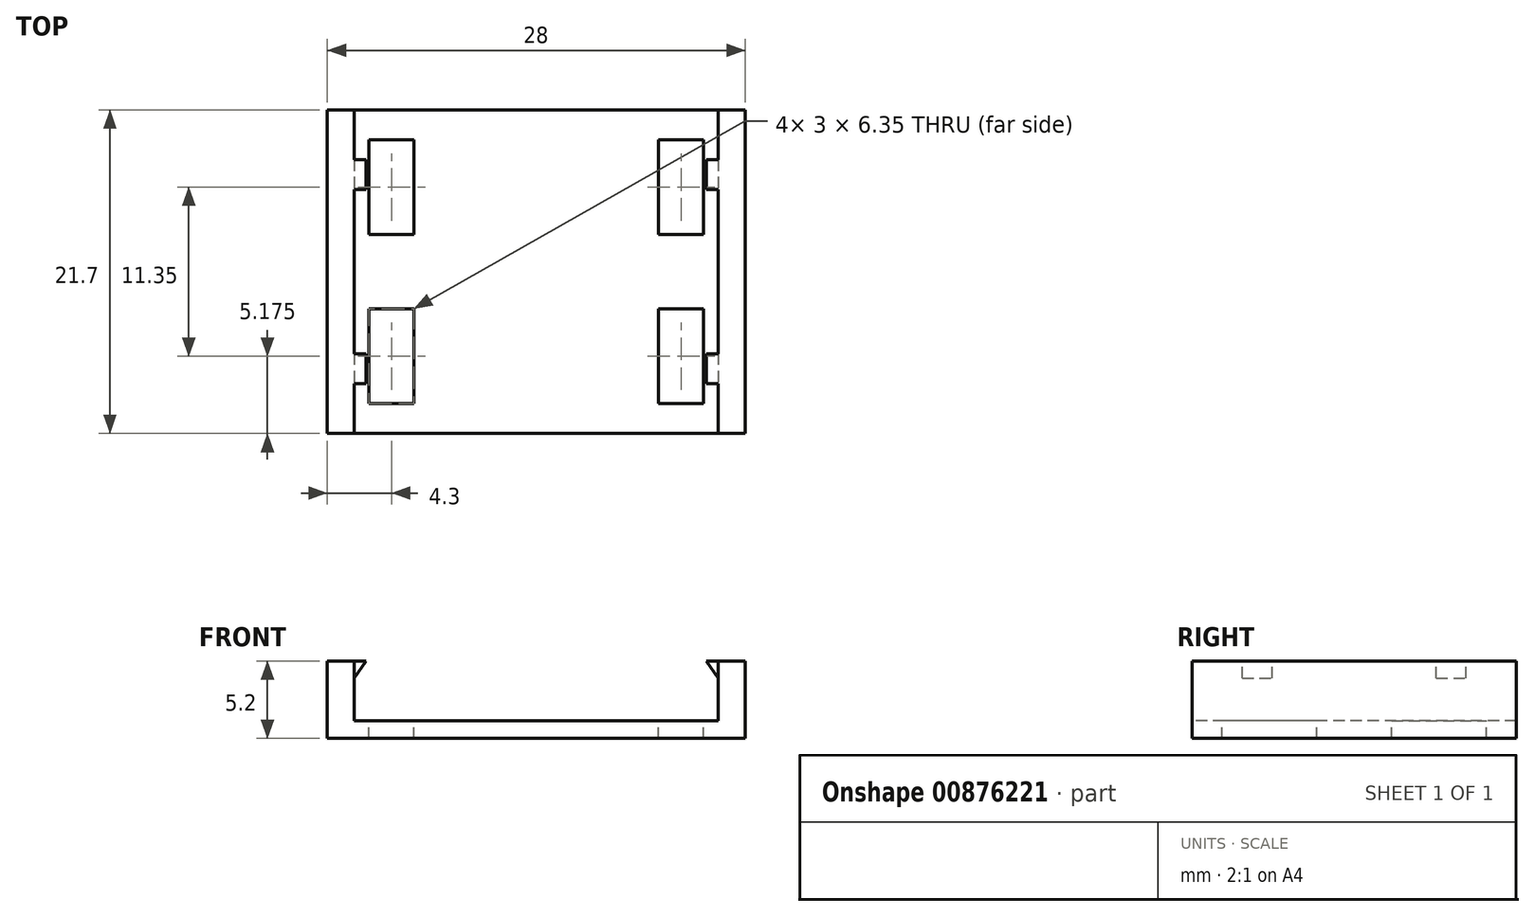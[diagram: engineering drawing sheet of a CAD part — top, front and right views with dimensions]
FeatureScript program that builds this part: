
annotation { "Feature Type Name" : "Feature", "Feature Type Description" : "" }
export const myFeature = defineFeature(function(context is Context, id is Id, definition is map)
    precondition{}
    {
        {
            var Q0;
            Q0=qCreatedBy(makeId("Top.planeOp"),FACE);
            var sketch = newSketch(context, id + "F0", { "sketchPlane" : qUnion([Q0])});
            skLineSegment(sketch, "E0.bottom", {"start": v(-14, 16.35) * mm, "end": v(14, 16.35) * mm});
            skLineSegment(sketch, "E0.top", {"start": v(-14, -16.35) * mm, "end": v(14, -16.35) * mm});
            skLineSegment(sketch, "E0.left", {"start": v(-14, 16.35) * mm, "end": v(-14, -16.35) * mm});
            skLineSegment(sketch, "E0.right", {"start": v(14, 16.35) * mm, "end": v(14, -16.35) * mm});
            skPoint(sketch, "E0.middle", {"position": v(0, 0) * mm});
            skSolve(sketch);
        }
        {
            var Q0;
            Q0=makeQuery(id+"F0.imprint","IMPRINT",FACE,{"disambiguationData":[TD([[makeQuery(id+"F0.imprint","IMPRINT",EDGE,{"derivedFrom":sQuery(id+"F0.wireOp",EDGE,"E0.bottom")}),-1.0]])]});
            extrude(context, id + "F1", {"entities" : qUnion([Q0]), "depth" : 1.2 * mm});
        }
        {
            var Q0;
            {var subQ5=sQuery(id+"F0.wireOp",EDGE,"E0.right");var subQ6=sQuery(id+"F0.wireOp",EDGE,"E0.left");var subQ7=sQuery(id+"F0.wireOp",EDGE,"E0.top");var subQ8=sQuery(id+"F0.wireOp",EDGE,"E0.bottom");var subQ9=makeQuery(id+"F1.opExtrude","CAP_FACE",FACE,{"disambiguationData":[OSD([subQ8,subQ7,subQ6,subQ5])],"isStart":false});var subQ12=subQ9;Q0=makeQuery(id+"FTskU3KK5imesQs_1.opFillet","MERGE",FACE,{"derivedFrom":[makeQuery(id+"FZi3CJKkktuihJ1_1.boolean.opBoolean","SPLIT",FACE,{"disambiguationData":[TD([makeQuery(id+"F1.opExtrude","SWEPT_FACE",FACE,{"disambiguationData":[OSD([subQ8])]})])],"derivedFrom":subQ12}),makeQuery(id+"FZ7EBSF1tdb4njM_1.boolean.opBoolean","MERGE",FACE,{"derivedFrom":[makeQuery(id+"FZi3CJKkktuihJ1_1.boolean.opBoolean","SPLIT",FACE,{"disambiguationData":[TD([makeQuery(id+"FlsG0jWeIkAughT_1.opExtrude","SWEPT_FACE",FACE,{"disambiguationData":[OSD([sQuery(id+"F5Wyuop6bpOGen8_1.wireOp",EDGE,"vaNtV44L-idVL-UOBQ-HHhe-vYpkaX2QMto8.bottom")])]})])],"derivedFrom":subQ12}),makeQuery(id+"FZ7EBSF1tdb4njM_1.opExtrude","CAP_FACE",FACE,{"disambiguationData":[OSD([sQuery(id+"FoSm93bD1NxVTFu_1.wireOp",EDGE,"97a7e462-43fe-4127-a601-1d90c2ab95a00.MirrorCS"),sQuery(id+"FoSm93bD1NxVTFu_1.wireOp",EDGE,"97a7e462-43fe-4127-a601-1d90c2ab95a01.MirrorCS"),sQuery(id+"FoSm93bD1NxVTFu_1.wireOp",EDGE,"97a7e462-43fe-4127-a601-1d90c2ab95a02.MirrorCS"),sQuery(id+"FoSm93bD1NxVTFu_1.wireOp",EDGE,"97a7e462-43fe-4127-a601-1d90c2ab95a03.MirrorCS")])],"isStart":false})]}),makeQuery(id+"FZ7EBSF1tdb4njM_1.boolean.opBoolean","MERGE",FACE,{"derivedFrom":[makeQuery(id+"FZi3CJKkktuihJ1_1.boolean.opBoolean","SPLIT",FACE,{"disambiguationData":[TD([makeQuery(id+"FlsG0jWeIkAughT_1.opExtrude","SWEPT_FACE",FACE,{"disambiguationData":[OSD([sQuery(id+"F5Wyuop6bpOGen8_1.wireOp",EDGE,"5b2c8ccd-c1e1-48dd-aecc-73c440124aab0.MirrorCS")])]})])],"derivedFrom":subQ12}),makeQuery(id+"FZ7EBSF1tdb4njM_1.opExtrude","CAP_FACE",FACE,{"disambiguationData":[OSD([sQuery(id+"FoSm93bD1NxVTFu_1.wireOp",EDGE,"85c03d27-702a-4580-8be8-e1d3315b53173.MirrorCS"),sQuery(id+"FoSm93bD1NxVTFu_1.wireOp",EDGE,"85c03d27-702a-4580-8be8-e1d3315b53174.MirrorCS"),sQuery(id+"FoSm93bD1NxVTFu_1.wireOp",EDGE,"85c03d27-702a-4580-8be8-e1d3315b53176.MirrorCS"),sQuery(id+"FoSm93bD1NxVTFu_1.wireOp",EDGE,"85c03d27-702a-4580-8be8-e1d3315b53177.MirrorCS")])],"isStart":false})]})]});}
            var sketch = newSketch(context, id + "F2", { "sketchPlane" : qUnion([Q0])});
            skLineSegment(sketch, "E1.bottom", {"start": v(-12.2, 15.35) * mm, "end": v(12.2, 15.35) * mm});
            skLineSegment(sketch, "E1.top", {"start": v(-12.2, -15.35) * mm, "end": v(12.2, -15.35) * mm});
            skLineSegment(sketch, "E1.left", {"start": v(-12.2, 15.35) * mm, "end": v(-12.2, -15.35) * mm});
            skLineSegment(sketch, "E1.right", {"start": v(12.2, 15.35) * mm, "end": v(12.2, -15.35) * mm});
            skPoint(sketch, "E1.middle", {"position": v(0, 0) * mm});
            skSolve(sketch);
        }
        {
            var Q0;
            Q0=makeQuery(id+"F2.imprint","IMPRINT",FACE,{"disambiguationData":[TD([[makeQuery(id+"F2.imprint","IMPRINT",EDGE,{"derivedFrom":sQuery(id+"F2.wireOp",EDGE,"E1.bottom")}),1.0]])]});
            extrude(context, id + "F3", {"entities" : qUnion([Q0]), "operationType" : NewBodyOperationType.ADD, "depth" : 4 * mm});
        }
        {
            var Q0;
            Q0=makeQuery(id+"F3.opExtrude","CAP_FACE",FACE,{"disambiguationData":[OSD([sQuery(id+"F0.wireOp",EDGE,"E0.bottom"),sQuery(id+"F0.wireOp",EDGE,"E0.top"),sQuery(id+"F0.wireOp",EDGE,"E0.left"),sQuery(id+"F0.wireOp",EDGE,"E0.right"),sQuery(id+"F2.wireOp",EDGE,"E1.bottom"),sQuery(id+"F2.wireOp",EDGE,"E1.top"),sQuery(id+"F2.wireOp",EDGE,"E1.left"),sQuery(id+"F2.wireOp",EDGE,"E1.right")])],"isStart":false});
            var sketch = newSketch(context, id + "F4", { "sketchPlane" : qUnion([Q0])});
            skLineSegment(sketch, "E2.bottom", {"start": v(-14, -16.35) * mm, "end": v(14, -16.35) * mm});
            skLineSegment(sketch, "E2.top", {"start": v(-14, -10.85) * mm, "end": v(14, -10.85) * mm});
            skLineSegment(sketch, "E2.left", {"start": v(-14, -16.35) * mm, "end": v(-14, -10.85) * mm});
            skLineSegment(sketch, "E2.right", {"start": v(14, -16.35) * mm, "end": v(14, -10.85) * mm});
            skLineSegment(sketch, "E3.MirrorCS", {"start": v(14, 16.35) * mm, "end": v(14, 10.85) * mm});
            skLineSegment(sketch, "E4.MirrorCS", {"start": v(-14, 16.35) * mm, "end": v(-14, 10.85) * mm});
            skLineSegment(sketch, "E5.MirrorCS", {"start": v(-14, 16.35) * mm, "end": v(14, 16.35) * mm});
            skLineSegment(sketch, "E6.MirrorCS", {"start": v(-14, 10.85) * mm, "end": v(14, 10.85) * mm});
            skSolve(sketch);
        }
        {
            var Q0;
            Q0=qSketchRegion(id+"F4",true);
            extrude(context, id + "F5", {"entities" : qUnion([Q0]), "operationType" : NewBodyOperationType.REMOVE, "endBound" : BoundingType.THROUGH_ALL, "oppositeDirection" : true, "depth" : 25 * mm});
        }
        {
            var Q0;
            {var subQ5=sQuery(id+"F0.wireOp",EDGE,"E0.right");var subQ6=sQuery(id+"F0.wireOp",EDGE,"E0.left");var subQ7=sQuery(id+"F0.wireOp",EDGE,"E0.top");var subQ8=sQuery(id+"F0.wireOp",EDGE,"E0.bottom");var subQ9=makeQuery(id+"F1.opExtrude","CAP_FACE",FACE,{"disambiguationData":[OSD([subQ8,subQ7,subQ6,subQ5])],"isStart":false});var subQ12=subQ9;Q0=makeQuery(id+"FTskU3KK5imesQs_1.opFillet","MERGE",FACE,{"derivedFrom":[makeQuery(id+"FZi3CJKkktuihJ1_1.boolean.opBoolean","SPLIT",FACE,{"disambiguationData":[TD([makeQuery(id+"F1.opExtrude","SWEPT_FACE",FACE,{"disambiguationData":[OSD([subQ8])]})])],"derivedFrom":subQ12}),makeQuery(id+"FZ7EBSF1tdb4njM_1.boolean.opBoolean","MERGE",FACE,{"derivedFrom":[makeQuery(id+"FZi3CJKkktuihJ1_1.boolean.opBoolean","SPLIT",FACE,{"disambiguationData":[TD([makeQuery(id+"FlsG0jWeIkAughT_1.opExtrude","SWEPT_FACE",FACE,{"disambiguationData":[OSD([sQuery(id+"F5Wyuop6bpOGen8_1.wireOp",EDGE,"vaNtV44L-idVL-UOBQ-HHhe-vYpkaX2QMto8.bottom")])]})])],"derivedFrom":subQ12}),makeQuery(id+"FZ7EBSF1tdb4njM_1.opExtrude","CAP_FACE",FACE,{"disambiguationData":[OSD([sQuery(id+"FoSm93bD1NxVTFu_1.wireOp",EDGE,"97a7e462-43fe-4127-a601-1d90c2ab95a00.MirrorCS"),sQuery(id+"FoSm93bD1NxVTFu_1.wireOp",EDGE,"97a7e462-43fe-4127-a601-1d90c2ab95a01.MirrorCS"),sQuery(id+"FoSm93bD1NxVTFu_1.wireOp",EDGE,"97a7e462-43fe-4127-a601-1d90c2ab95a02.MirrorCS"),sQuery(id+"FoSm93bD1NxVTFu_1.wireOp",EDGE,"97a7e462-43fe-4127-a601-1d90c2ab95a03.MirrorCS")])],"isStart":false})]}),makeQuery(id+"FZ7EBSF1tdb4njM_1.boolean.opBoolean","MERGE",FACE,{"derivedFrom":[makeQuery(id+"FZi3CJKkktuihJ1_1.boolean.opBoolean","SPLIT",FACE,{"disambiguationData":[TD([makeQuery(id+"FlsG0jWeIkAughT_1.opExtrude","SWEPT_FACE",FACE,{"disambiguationData":[OSD([sQuery(id+"F5Wyuop6bpOGen8_1.wireOp",EDGE,"5b2c8ccd-c1e1-48dd-aecc-73c440124aab0.MirrorCS")])]})])],"derivedFrom":subQ12}),makeQuery(id+"FZ7EBSF1tdb4njM_1.opExtrude","CAP_FACE",FACE,{"disambiguationData":[OSD([sQuery(id+"FoSm93bD1NxVTFu_1.wireOp",EDGE,"85c03d27-702a-4580-8be8-e1d3315b53173.MirrorCS"),sQuery(id+"FoSm93bD1NxVTFu_1.wireOp",EDGE,"85c03d27-702a-4580-8be8-e1d3315b53174.MirrorCS"),sQuery(id+"FoSm93bD1NxVTFu_1.wireOp",EDGE,"85c03d27-702a-4580-8be8-e1d3315b53176.MirrorCS"),sQuery(id+"FoSm93bD1NxVTFu_1.wireOp",EDGE,"85c03d27-702a-4580-8be8-e1d3315b53177.MirrorCS")])],"isStart":false})]})]});}
            var sketch = newSketch(context, id + "F6", { "sketchPlane" : qUnion([Q0])});
            skLineSegment(sketch, "E7.bottom", {"start": v(-12.2, -5.25) * mm, "end": v(-10.2, -5.25) * mm});
            skLineSegment(sketch, "E7.top", {"start": v(-12.2, 5.25) * mm, "end": v(-10.2, 5.25) * mm});
            skLineSegment(sketch, "E7.left", {"start": v(-12.2, -5.25) * mm, "end": v(-12.2, 5.25) * mm});
            skLineSegment(sketch, "E7.right", {"start": v(12.2, -5.25) * mm, "end": v(12.2, 5.25) * mm});
            skLineSegment(sketch, "E8.bottom", {"start": v(-12.2, -7.25) * mm, "end": v(-10.2, -7.25) * mm});
            skLineSegment(sketch, "E8.top", {"start": v(-12.2, -10.85) * mm, "end": v(-10.2, -10.85) * mm});
            skLineSegment(sketch, "E8.left", {"start": v(-12.2, -7.25) * mm, "end": v(-12.2, -10.85) * mm});
            skLineSegment(sketch, "E8.right", {"start": v(12.2, -7.25) * mm, "end": v(12.2, -10.85) * mm});
            skLineSegment(sketch, "E9.MirrorCS", {"start": v(-12.2, 7.25) * mm, "end": v(-10.2, 7.25) * mm});
            skLineSegment(sketch, "E10.MirrorCS", {"start": v(-12.2, 10.85) * mm, "end": v(12.2, 10.85) * mm});
            skLineSegment(sketch, "E11.MirrorCS", {"start": v(12.2, 7.25) * mm, "end": v(12.2, 10.85) * mm});
            skLineSegment(sketch, "E12.MirrorCS", {"start": v(-12.2, 7.25) * mm, "end": v(-12.2, 10.85) * mm});
            skLineSegment(sketch, "E13", {"start": v(-10.2, -10.85) * mm, "end": v(-10.2, -7.25) * mm});
            skLineSegment(sketch, "E14.MirrorCS", {"start": v(10.2, -10.85) * mm, "end": v(10.2, -7.25) * mm});
            skLineSegment(sketch, "E15.trimOffspring", {"start": v(-10.2, -5.25) * mm, "end": v(-10.2, 5.25) * mm});
            skLineSegment(sketch, "E16.trimOffspring", {"start": v(10.2, -7.25) * mm, "end": v(12.2, -7.25) * mm});
            skLineSegment(sketch, "E17.trimOffspring", {"start": v(10.2, -10.85) * mm, "end": v(12.2, -10.85) * mm});
            skLineSegment(sketch, "E18.trimOffspring", {"start": v(10.2, -5.25) * mm, "end": v(12.2, -5.25) * mm});
            skLineSegment(sketch, "E19.trimOffspring", {"start": v(10.2, 5.25) * mm, "end": v(12.2, 5.25) * mm});
            skLineSegment(sketch, "E20.trimOffspring", {"start": v(10.2, 7.25) * mm, "end": v(12.2, 7.25) * mm});
            skLineSegment(sketch, "E21.trimOffspring", {"start": v(-10.2, 7.25) * mm, "end": v(-10.2, 10.85) * mm});
            skLineSegment(sketch, "E22.trimOffspring", {"start": v(10.2, -5.25) * mm, "end": v(10.2, 5.25) * mm});
            skLineSegment(sketch, "E23.trimOffspring", {"start": v(10.2, 7.25) * mm, "end": v(10.2, 10.85) * mm});
            skSolve(sketch);
        }
        {
            var Q0;
            Q0=makeQuery(id+"F6.imprint","IMPRINT",FACE,{"disambiguationData":[TD([[makeQuery(id+"F6.imprint","IMPRINT",EDGE,{"derivedFrom":sQuery(id+"F6.wireOp",EDGE,"E8.bottom")}),-1.0]])]});
            var Q1;
            Q1=makeQuery(id+"F6.imprint","IMPRINT",FACE,{"disambiguationData":[TD([[makeQuery(id+"F6.imprint","IMPRINT",EDGE,{"derivedFrom":sQuery(id+"F6.wireOp",EDGE,"E7.bottom")}),1.0]])]});
            var Q2;
            Q2=makeQuery(id+"F6.imprint","IMPRINT",FACE,{"disambiguationData":[TD([[makeQuery(id+"F6.imprint","IMPRINT",EDGE,{"derivedFrom":sQuery(id+"F6.wireOp",EDGE,"E9.MirrorCS")}),1.0]])]});
            var Q3;
            Q3=makeQuery(id+"F6.imprint","IMPRINT",FACE,{"disambiguationData":[TD([[makeQuery(id+"F6.imprint","IMPRINT",EDGE,{"derivedFrom":sQuery(id+"F6.wireOp",EDGE,"E8.right")}),-1.0]])]});
            var Q4;
            Q4=makeQuery(id+"F6.imprint","IMPRINT",FACE,{"disambiguationData":[TD([[makeQuery(id+"F6.imprint","IMPRINT",EDGE,{"derivedFrom":sQuery(id+"F6.wireOp",EDGE,"E7.right")}),-1.0]])]});
            var Q5;
            {var subQ0=sQuery(id+"F6.wireOp",EDGE,"E11.MirrorCS");Q5=makeQuery(id+"F6.imprint","IMPRINT",FACE,{"disambiguationData":[TD([[makeQuery(id+"F6.imprint","IMPRINT",EDGE,{"derivedFrom":subQ0}),-1.0]])]});}
            extrude(context, id + "F7", {"entities" : qUnion([Q0, Q1, Q2, Q3, Q4, Q5]), "operationType" : NewBodyOperationType.REMOVE, "depth" : 30 * mm});
        }
        {
            var Q0;
            Q0=makeQuery(id+"F5.boolean.opBoolean","COPY",FACE,{"derivedFrom":makeQuery(id+"F5.opExtrude","SWEPT_FACE",FACE,{"disambiguationData":[OSD([sQuery(id+"F4.wireOp",EDGE,"E6.MirrorCS")])]})});
            var sketch = newSketch(context, id + "F8", { "sketchPlane" : qUnion([Q0])});
            skLineSegment(sketch, "E24", {"start": v(-12.2, 5.2) * mm, "end": v(-11.4, 5.2) * mm});
            skLineSegment(sketch, "E25", {"start": v(-11.4, 5.2) * mm, "end": v(-12.2, 4.06) * mm});
            skLineSegment(sketch, "E26", {"start": v(-12.2, 4.06) * mm, "end": v(-12.2, 5.2) * mm});
            skLineSegment(sketch, "E27.MirrorCS", {"start": v(12.2, 5.2) * mm, "end": v(11.4, 5.2) * mm});
            skLineSegment(sketch, "E28.MirrorCS", {"start": v(11.4, 5.2) * mm, "end": v(12.2, 4.06) * mm});
            skLineSegment(sketch, "E29.MirrorCS", {"start": v(12.2, 4.06) * mm, "end": v(12.2, 5.2) * mm});
            skSolve(sketch);
        }
        {
            var Q0;
            Q0=makeQuery(id+"F8.imprint","IMPRINT",FACE,{"disambiguationData":[TD([[makeQuery(id+"F8.imprint","IMPRINT",EDGE,{"derivedFrom":sQuery(id+"F8.wireOp",EDGE,"E24")}),-1.0]])]});
            var Q1;
            Q1=makeQuery(id+"F8.imprint","IMPRINT",FACE,{"disambiguationData":[TD([[makeQuery(id+"F8.imprint","IMPRINT",EDGE,{"derivedFrom":sQuery(id+"F8.wireOp",EDGE,"E27.MirrorCS")}),1.0]])]});
            var Q2;
            Q2=makeQuery(id+"F5.boolean.opBoolean","COPY",FACE,{"derivedFrom":makeQuery(id+"F5.opExtrude","SWEPT_FACE",FACE,{"disambiguationData":[OSD([sQuery(id+"F4.wireOp",EDGE,"E2.top")])]})});
            extrude(context, id + "F9", {"entities" : qUnion([Q0, Q1]), "operationType" : NewBodyOperationType.ADD, "endBound" : BoundingType.UP_TO_SURFACE, "oppositeDirection" : true, "endBoundEntityFace" : qUnion([Q2]), "depth" : 25 * mm});
        }
        {
            var Q0;
            {var subQ0=sQuery(id+"F0.wireOp",EDGE,"E0.right");var subQ1=sQuery(id+"F2.wireOp",EDGE,"E1.right");Q0=makeQuery(id+"F9.boolean.opBoolean","MERGE",FACE,{"derivedFrom":[makeQuery(id+"F5.boolean.opBoolean","SPLIT",FACE,{"disambiguationData":[TD([makeQuery(id+"F1.opExtrude","SWEPT_FACE",FACE,{"disambiguationData":[OSD([subQ0])]})])],"derivedFrom":makeQuery(id+"F3.opExtrude","CAP_FACE",FACE,{"disambiguationData":[OSD([sQuery(id+"F0.wireOp",EDGE,"E0.bottom"),sQuery(id+"F0.wireOp",EDGE,"E0.top"),sQuery(id+"F0.wireOp",EDGE,"E0.left"),subQ0,sQuery(id+"F2.wireOp",EDGE,"E1.bottom"),sQuery(id+"F2.wireOp",EDGE,"E1.top"),sQuery(id+"F2.wireOp",EDGE,"E1.left"),subQ1])],"isStart":false})}),makeQuery(id+"F9.opExtrude","SWEPT_FACE",FACE,{"disambiguationData":[OSD([sQuery(id+"F8.wireOp",EDGE,"E24")])]})]});}
            var sketch = newSketch(context, id + "F10", { "sketchPlane" : qUnion([Q0])});
            skLineSegment(sketch, "E30.bottom", {"start": v(12.2, 5.5) * mm, "end": v(-12.2, 5.5) * mm});
            skLineSegment(sketch, "E30.top", {"start": v(12.2, -5.5) * mm, "end": v(-12.2, -5.5) * mm});
            skLineSegment(sketch, "E30.left", {"start": v(12.2, 5.5) * mm, "end": v(12.2, -5.5) * mm});
            skLineSegment(sketch, "E30.right", {"start": v(-12.2, 5.5) * mm, "end": v(-12.2, -5.5) * mm});
            skPoint(sketch, "E30.middle", {"position": v(0, 0) * mm});
            skLineSegment(sketch, "E31.bottom", {"start": v(12.2, 10.85) * mm, "end": v(-12.2, 10.85) * mm});
            skLineSegment(sketch, "E31.top", {"start": v(12.2, 7.5) * mm, "end": v(-12.2, 7.5) * mm});
            skLineSegment(sketch, "E31.left", {"start": v(12.2, 10.85) * mm, "end": v(12.2, 7.5) * mm});
            skLineSegment(sketch, "E31.right", {"start": v(-12.2, 10.85) * mm, "end": v(-12.2, 7.5) * mm});
            skPoint(sketch, "E31.middle", {"position": v(0, 9.18) * mm});
            skLineSegment(sketch, "E32.MirrorCS", {"start": v(12.2, -7.5) * mm, "end": v(-12.2, -7.5) * mm});
            skLineSegment(sketch, "E33.MirrorCS", {"start": v(12.2, -10.85) * mm, "end": v(12.2, -7.5) * mm});
            skLineSegment(sketch, "E34.MirrorCS", {"start": v(-12.2, -10.85) * mm, "end": v(-12.2, -7.5) * mm});
            skPoint(sketch, "E35.MirrorP", {"position": v(0, -9.18) * mm});
            skLineSegment(sketch, "E36.MirrorCS", {"start": v(12.2, -10.85) * mm, "end": v(-12.2, -10.85) * mm});
            skSolve(sketch);
        }
        {
            var Q0;
            Q0=qSketchRegion(id+"F10",true);
            extrude(context, id + "F11", {"entities" : qUnion([Q0]), "operationType" : NewBodyOperationType.REMOVE, "oppositeDirection" : true, "depth" : 3 * mm});
        }
        {
            var Q0;
            Q0=makeQuery(id+"F1.opExtrude","CAP_FACE",FACE,{"disambiguationData":[OSD([sQuery(id+"F0.wireOp",EDGE,"E0.bottom"),sQuery(id+"F0.wireOp",EDGE,"E0.top"),sQuery(id+"F0.wireOp",EDGE,"E0.left"),sQuery(id+"F0.wireOp",EDGE,"E0.right")])],"isStart":false});
            var sketch = newSketch(context, id + "F12", { "sketchPlane" : qUnion([Q0])});
            skLineSegment(sketch, "E37.bottom", {"start": v(-8.2, 2.5) * mm, "end": v(-11.2, 2.5) * mm});
            skLineSegment(sketch, "E37.top", {"start": v(-8.2, 8.85) * mm, "end": v(-11.2, 8.85) * mm});
            skLineSegment(sketch, "E37.left", {"start": v(-8.2, 2.5) * mm, "end": v(-8.2, 8.85) * mm});
            skLineSegment(sketch, "E37.right", {"start": v(-11.2, 2.5) * mm, "end": v(-11.2, 8.85) * mm});
            skPoint(sketch, "E37.middle", {"position": v(-9.7, 5.68) * mm});
            skLineSegment(sketch, "E38.MirrorCS", {"start": v(-8.2, -8.85) * mm, "end": v(-11.2, -8.85) * mm});
            skLineSegment(sketch, "E39.MirrorCS", {"start": v(-8.2, -2.5) * mm, "end": v(-11.2, -2.5) * mm});
            skLineSegment(sketch, "E40.MirrorCS", {"start": v(-8.2, -2.5) * mm, "end": v(-8.2, -8.85) * mm});
            skLineSegment(sketch, "E41.MirrorCS", {"start": v(-11.2, -2.5) * mm, "end": v(-11.2, -8.85) * mm});
            skPoint(sketch, "E42.MirrorP", {"position": v(-9.7, -5.68) * mm});
            skLineSegment(sketch, "E43.MirrorCS", {"start": v(8.2, -2.5) * mm, "end": v(11.2, -2.5) * mm});
            skPoint(sketch, "E44.MirrorP", {"position": v(9.7, 5.68) * mm});
            skLineSegment(sketch, "E45.MirrorCS", {"start": v(8.2, -8.85) * mm, "end": v(11.2, -8.85) * mm});
            skLineSegment(sketch, "E46.MirrorCS", {"start": v(8.2, 2.5) * mm, "end": v(11.2, 2.5) * mm});
            skLineSegment(sketch, "E47.MirrorCS", {"start": v(8.2, 8.85) * mm, "end": v(11.2, 8.85) * mm});
            skLineSegment(sketch, "E48.MirrorCS", {"start": v(11.2, -2.5) * mm, "end": v(11.2, -8.85) * mm});
            skLineSegment(sketch, "E49.MirrorCS", {"start": v(8.2, -2.5) * mm, "end": v(8.2, -8.85) * mm});
            skLineSegment(sketch, "E50.MirrorCS", {"start": v(11.2, 2.5) * mm, "end": v(11.2, 8.85) * mm});
            skLineSegment(sketch, "E51.MirrorCS", {"start": v(8.2, 2.5) * mm, "end": v(8.2, 8.85) * mm});
            skPoint(sketch, "E52.MirrorP", {"position": v(9.7, -5.68) * mm});
            skSolve(sketch);
        }
        {
            var Q0;
            Q0=makeQuery(id+"F12.imprint","IMPRINT",FACE,{"disambiguationData":[TD([[makeQuery(id+"F12.imprint","IMPRINT",EDGE,{"derivedFrom":sQuery(id+"F12.wireOp",EDGE,"E37.bottom")}),-1.0]])]});
            var Q1;
            Q1=makeQuery(id+"F12.imprint","IMPRINT",FACE,{"disambiguationData":[TD([[makeQuery(id+"F12.imprint","IMPRINT",EDGE,{"derivedFrom":sQuery(id+"F12.wireOp",EDGE,"E38.MirrorCS")}),-1.0]])]});
            var Q2;
            Q2=makeQuery(id+"F12.imprint","IMPRINT",FACE,{"disambiguationData":[TD([[makeQuery(id+"F12.imprint","IMPRINT",EDGE,{"derivedFrom":sQuery(id+"F12.wireOp",EDGE,"E46.MirrorCS")}),1.0]])]});
            var Q3;
            Q3=makeQuery(id+"F12.imprint","IMPRINT",FACE,{"disambiguationData":[TD([[makeQuery(id+"F12.imprint","IMPRINT",EDGE,{"derivedFrom":sQuery(id+"F12.wireOp",EDGE,"E43.MirrorCS")}),-1.0]])]});
            extrude(context, id + "F13", {"entities" : qUnion([Q0, Q1, Q2, Q3]), "operationType" : NewBodyOperationType.REMOVE, "oppositeDirection" : true, "depth" : 25 * mm});
        }
    });
